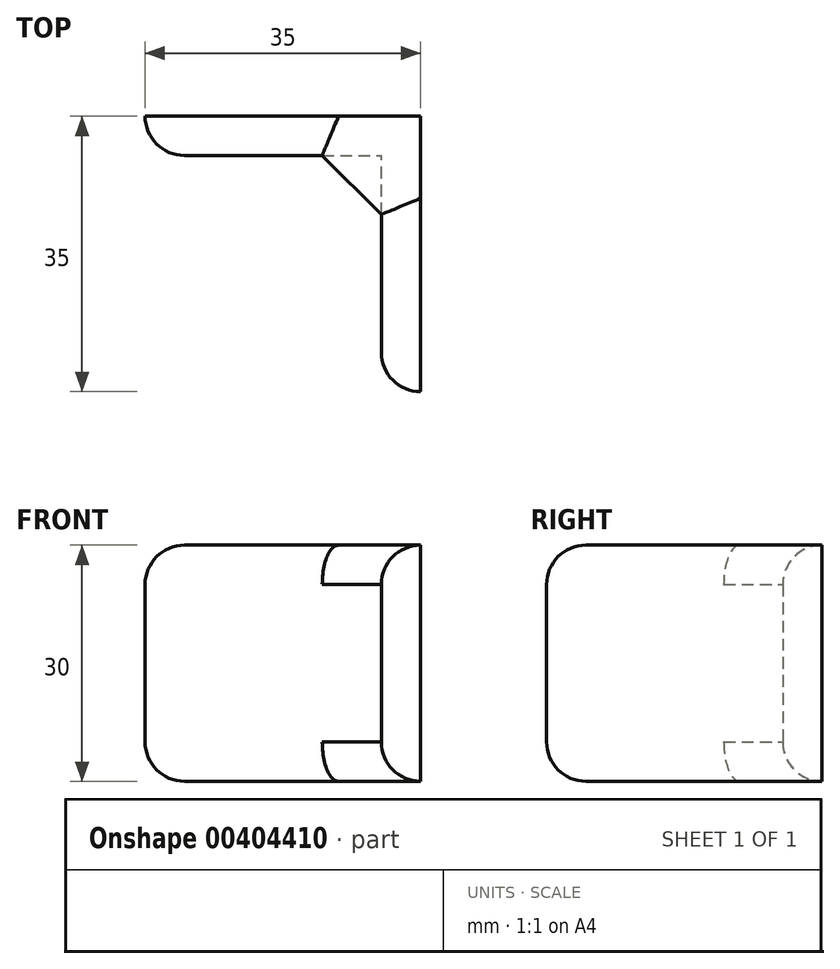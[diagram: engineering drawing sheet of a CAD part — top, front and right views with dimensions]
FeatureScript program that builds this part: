
annotation { "Feature Type Name" : "Feature", "Feature Type Description" : "" }
export const myFeature = defineFeature(function(context is Context, id is Id, definition is map)
    precondition{}
    {
        {
            var Q0;
            Q0=qCreatedBy(makeId("Front.planeOp"),FACE);
            var sketch = newSketch(context, id + "F0", { "sketchPlane" : qUnion([Q0])});
            skLineSegment(sketch, "E0.bottom", {"start": v(-19.46, -1.02) * mm, "end": v(15.54, -1.02) * mm});
            skLineSegment(sketch, "E0.top", {"start": v(-19.46, -21.02) * mm, "end": v(15.54, -21.02) * mm});
            skLineSegment(sketch, "E0.left", {"start": v(-19.46, -1.02) * mm, "end": v(-19.46, -21.02) * mm});
            skLineSegment(sketch, "E0.right", {"start": v(15.54, -1.02) * mm, "end": v(15.54, -21.02) * mm});
            skSolve(sketch);
        }
        {
            var Q0;
            Q0=makeQuery(id+"F0.imprint","IMPRINT",FACE,{"disambiguationData":[TD([[makeQuery(id+"F0.imprint","IMPRINT",EDGE,{"derivedFrom":sQuery(id+"F0.wireOp",EDGE,"E0.bottom")}),-1.0]])]});
            extrude(context, id + "F1", {"entities" : qUnion([Q0]), "depth" : 5 * mm});
        }
        {
            var Q0;
            Q0=makeQuery(id+"F1.opExtrude","CAP_FACE",FACE,{"disambiguationData":[OSD([sQuery(id+"F0.wireOp",EDGE,"E0.bottom"),sQuery(id+"F0.wireOp",EDGE,"E0.top"),sQuery(id+"F0.wireOp",EDGE,"E0.left"),sQuery(id+"F0.wireOp",EDGE,"E0.right")])],"isStart":false});
            var sketch = newSketch(context, id + "F2", { "sketchPlane" : qUnion([Q0])});
            skLineSegment(sketch, "E1.bottom", {"start": v(15.54, -1.02) * mm, "end": v(10.54, -1.02) * mm});
            skLineSegment(sketch, "E1.top", {"start": v(15.54, -21.02) * mm, "end": v(10.54, -21.02) * mm});
            skLineSegment(sketch, "E1.left", {"start": v(15.54, -1.02) * mm, "end": v(15.54, -21.02) * mm});
            skLineSegment(sketch, "E1.right", {"start": v(10.54, -1.02) * mm, "end": v(10.54, -21.02) * mm});
            skSolve(sketch);
        }
        {
            var Q0;
            Q0=makeQuery(id+"F2.imprint","IMPRINT",FACE,{"disambiguationData":[TD([[makeQuery(id+"F2.imprint","IMPRINT",EDGE,{"derivedFrom":sQuery(id+"F2.wireOp",EDGE,"E1.bottom")}),-1.0]])]});
            extrude(context, id + "F3", {"entities" : qUnion([Q0]), "operationType" : NewBodyOperationType.ADD, "depth" : 30 * mm});
        }
        {
            var Q0;
            Q0=makeQuery(id+"F1.opExtrude","CAP_EDGE",EDGE,{"disambiguationData":[OSD([sQuery(id+"F0.wireOp",EDGE,"E0.left")])],"isStart":false});
            var Q1;
            Q1=makeQuery(id+"F3.opExtrude","CAP_EDGE",EDGE,{"disambiguationData":[OSD([sQuery(id+"F2.wireOp",EDGE,"E1.right")])],"isStart":false});
            fillet(context, id + "F4", {"entities" : qUnion([Q0, Q1]), "radius" : 5 * mm, "tangentPropagation" : true, "allowEdgeOverflow" : false});
        }
        {
            var Q0;
            Q0=makeQuery(id+"F3.boolean.opBoolean","MERGE",FACE,{"derivedFrom":[makeQuery(id+"F1.opExtrude","SWEPT_FACE",FACE,{"disambiguationData":[OSD([sQuery(id+"F0.wireOp",EDGE,"E0.bottom")])]}),makeQuery(id+"F3.opExtrude","SWEPT_FACE",FACE,{"disambiguationData":[OSD([sQuery(id+"F2.wireOp",EDGE,"E1.bottom")])]})]});
            var sketch = newSketch(context, id + "F5", { "sketchPlane" : qUnion([Q0])});
            skLineSegment(sketch, "E2", {"start": v(15.54, 0) * mm, "end": v(-1.96, 0) * mm});
            skLineSegment(sketch, "E3", {"start": v(-1.96, 0) * mm, "end": v(15.54, -17.5) * mm});
            skSolve(sketch);
        }
        {
            var Q0;
            {var subQ0=sQuery(id+"F5.wireOp",EDGE,"E3");var subQ1=sQuery(id+"F0.wireOp",EDGE,"E0.bottom");var subQ2=makeQuery(id+"F1.opExtrude","CAP_EDGE",EDGE,{"disambiguationData":[OSD([subQ1])],"isStart":false});var subQ3=makeQuery(id+"F5.imprint","INTERSECT",VERTEX,{"derivedFrom":[subQ2,subQ0]});Q0=makeQuery(id+"F5.imprint","IMPRINT",FACE,{"disambiguationData":[TD([[makeQuery(id+"F5.imprint","IMPRINT",EDGE,{"disambiguationData":[TD([[subQ3,-1.0]])],"derivedFrom":subQ0}),1.0]])]});}
            var Q1;
            {var subQ0=sQuery(id+"F5.wireOp",EDGE,"E2");Q1=makeQuery(id+"F5.imprint","IMPRINT",FACE,{"disambiguationData":[TD([[makeQuery(id+"F5.imprint","IMPRINT",EDGE,{"derivedFrom":subQ0}),-1.0]])]});}
            extrude(context, id + "F6", {"entities" : qUnion([Q0, Q1]), "operationType" : NewBodyOperationType.ADD, "depth" : 5 * mm});
        }
        {
            var Q0;
            {var subQ1=sQuery(id+"F0.wireOp",EDGE,"E0.left");var subQ4=sQuery(id+"F0.wireOp",EDGE,"E0.bottom");var subQ6=sQuery(id+"F2.wireOp",EDGE,"E1.bottom");Q0=makeQuery(id+"F6.boolean.opBoolean","SPLIT",FACE,{"disambiguationData":[TD([makeQuery(id+"F4.opFillet","BLEND_FACE",FACE,{"disambiguationData":[OSD([subQ1])]})])],"derivedFrom":makeQuery(id+"F3.boolean.opBoolean","MERGE",FACE,{"derivedFrom":[makeQuery(id+"F1.opExtrude","SWEPT_FACE",FACE,{"disambiguationData":[OSD([subQ4])]}),makeQuery(id+"F3.opExtrude","SWEPT_FACE",FACE,{"disambiguationData":[OSD([subQ6])]})]})});}
            extrude(context, id + "F7", {"entities" : qUnion([Q0]), "operationType" : NewBodyOperationType.ADD, "depth" : 5 * mm});
        }
        {
            var Q0;
            {var subQ2=sQuery(id+"F0.wireOp",EDGE,"E0.right");var subQ4=sQuery(id+"F2.wireOp",EDGE,"E1.bottom");var subQ5=sQuery(id+"F0.wireOp",EDGE,"E0.bottom");Q0=makeQuery(id+"F6.boolean.opBoolean","SPLIT",FACE,{"disambiguationData":[TD([makeQuery(id+"F1.opExtrude","SWEPT_FACE",FACE,{"disambiguationData":[OSD([subQ2])]})])],"derivedFrom":makeQuery(id+"F3.boolean.opBoolean","MERGE",FACE,{"derivedFrom":[makeQuery(id+"F1.opExtrude","SWEPT_FACE",FACE,{"disambiguationData":[OSD([subQ5])]}),makeQuery(id+"F3.opExtrude","SWEPT_FACE",FACE,{"disambiguationData":[OSD([subQ4])]})]})});}
            extrude(context, id + "F8", {"entities" : qUnion([Q0]), "operationType" : NewBodyOperationType.ADD, "depth" : 5 * mm});
        }
        {
            var Q0;
            Q0=makeQuery(id+"F6.opExtrude","CAP_EDGE",EDGE,{"disambiguationData":[OSD([sQuery(id+"F5.wireOp",EDGE,"E3")])],"isStart":false});
            var Q1;
            {var subQ0=sQuery(id+"F0.wireOp",EDGE,"E0.bottom");Q1=makeQuery(id+"F7.opExtrude","CAP_EDGE",EDGE,{"disambiguationData":[OSD([subQ0]),TDD([makeQuery(id+"F6.boolean.opBoolean","SPLIT",EDGE,{"disambiguationData":[topologyDisambiguationEdgeConnected([makeQuery(id+"F1.opExtrude","SWEPT_FACE",FACE,{"disambiguationData":[OSD([subQ0])]})])],"derivedFrom":makeQuery(id+"F1.opExtrude","CAP_EDGE",EDGE,{"disambiguationData":[OSD([subQ0])],"isStart":false})})])],"isStart":false});}
            var Q2;
            {var subQ0=sQuery(id+"F0.wireOp",EDGE,"E0.bottom");var subQ1=sQuery(id+"F2.wireOp",EDGE,"E1.bottom");var subQ2=sQuery(id+"F2.wireOp",EDGE,"E1.right");Q2=makeQuery(id+"F8.opExtrude","CAP_EDGE",EDGE,{"disambiguationData":[OSD([subQ0,subQ1,subQ2]),TDD([makeQuery(id+"F6.boolean.opBoolean","SPLIT",EDGE,{"disambiguationData":[topologyDisambiguationEdgeConnected([makeQuery(id+"F1.opExtrude","SWEPT_FACE",FACE,{"disambiguationData":[OSD([subQ0])]})])],"derivedFrom":makeQuery(id+"F3.opExtrude","SWEPT_EDGE",EDGE,{"disambiguationData":[OSD([subQ0,subQ1,subQ2])]})})])],"isStart":false});}
            fillet(context, id + "F9", {"entities" : qUnion([Q0, Q1, Q2]), "radius" : 5 * mm, "tangentPropagation" : true, "allowEdgeOverflow" : false});
        }
        {
            var Q0;
            Q0=makeQuery(id+"F3.boolean.opBoolean","MERGE",FACE,{"derivedFrom":[makeQuery(id+"F1.opExtrude","SWEPT_FACE",FACE,{"disambiguationData":[OSD([sQuery(id+"F0.wireOp",EDGE,"E0.top")])]}),makeQuery(id+"F3.opExtrude","SWEPT_FACE",FACE,{"disambiguationData":[OSD([sQuery(id+"F2.wireOp",EDGE,"E1.top")])]})]});
            var sketch = newSketch(context, id + "F10", { "sketchPlane" : qUnion([Q0])});
            skLineSegment(sketch, "E4", {"start": v(-1.96, 0) * mm, "end": v(15.54, 17.5) * mm});
            skSolve(sketch);
        }
        {
            var Q0;
            {var subQ1=sQuery(id+"F0.wireOp",EDGE,"E0.top");var subQ3=makeQuery(id+"F1.opExtrude","CAP_EDGE",EDGE,{"disambiguationData":[OSD([subQ1])],"isStart":true});var subQ5=sQuery(id+"F10.wireOp",EDGE,"E4");var subQ9=makeQuery(id+"F10.imprint","INTERSECT",VERTEX,{"derivedFrom":[subQ3,subQ5]});Q0=makeQuery(id+"F10.imprint","IMPRINT",FACE,{"disambiguationData":[TD([[makeQuery(id+"F10.imprint","IMPRINT",EDGE,{"disambiguationData":[TD([[subQ9,-1.0]])],"derivedFrom":subQ5}),-1.0]])]});}
            var Q1;
            {var subQ1=sQuery(id+"F0.wireOp",EDGE,"E0.top");var subQ6=makeQuery(id+"F4.opFillet","BLEND_EDGE",EDGE,{"blendedFrom":[makeQuery(id+"F1.opExtrude","CAP_EDGE",EDGE,{"disambiguationData":[OSD([sQuery(id+"F0.wireOp",EDGE,"E0.left")])],"isStart":false}),makeQuery(id+"F3.boolean.opBoolean","MERGE",FACE,{"derivedFrom":[makeQuery(id+"F1.opExtrude","SWEPT_FACE",FACE,{"disambiguationData":[OSD([subQ1])]}),makeQuery(id+"F3.opExtrude","SWEPT_FACE",FACE,{"disambiguationData":[OSD([sQuery(id+"F2.wireOp",EDGE,"E1.top")])]})]})],"blendedInto":[makeQuery(id+"F3.boolean.opBoolean","MERGE",FACE,{"derivedFrom":[makeQuery(id+"F1.opExtrude","SWEPT_FACE",FACE,{"disambiguationData":[OSD([subQ1])]}),makeQuery(id+"F3.opExtrude","SWEPT_FACE",FACE,{"disambiguationData":[OSD([sQuery(id+"F2.wireOp",EDGE,"E1.top")])]})]})]});Q1=makeQuery(id+"F10.imprint","IMPRINT",FACE,{"disambiguationData":[TD([[makeQuery(id+"F10.imprint","IMPRINT",EDGE,{"derivedFrom":subQ6}),1.0]])]});}
            var Q2;
            {var subQ0=sQuery(id+"F10.wireOp",EDGE,"E4");var subQ1=sQuery(id+"F0.wireOp",EDGE,"E0.top");var subQ2=makeQuery(id+"F1.opExtrude","CAP_EDGE",EDGE,{"disambiguationData":[OSD([subQ1])],"isStart":false});var subQ3=makeQuery(id+"F10.imprint","INTERSECT",VERTEX,{"derivedFrom":[subQ2,subQ0]});Q2=makeQuery(id+"F10.imprint","IMPRINT",FACE,{"disambiguationData":[TD([[makeQuery(id+"F10.imprint","IMPRINT",EDGE,{"disambiguationData":[TD([[subQ3,-1.0]])],"derivedFrom":subQ0}),-1.0]])]});}
            var Q3;
            {var subQ1=sQuery(id+"F2.wireOp",EDGE,"E1.top");var subQ2=sQuery(id+"F0.wireOp",EDGE,"E0.top");var subQ5=sQuery(id+"F2.wireOp",EDGE,"E1.right");var subQ8=makeQuery(id+"F4.opFillet","BLEND_EDGE",EDGE,{"blendedFrom":[makeQuery(id+"F3.opExtrude","CAP_EDGE",EDGE,{"disambiguationData":[OSD([subQ5])],"isStart":false}),makeQuery(id+"F3.boolean.opBoolean","MERGE",FACE,{"derivedFrom":[makeQuery(id+"F1.opExtrude","SWEPT_FACE",FACE,{"disambiguationData":[OSD([subQ2])]}),makeQuery(id+"F3.opExtrude","SWEPT_FACE",FACE,{"disambiguationData":[OSD([subQ1])]})]})],"blendedInto":[makeQuery(id+"F3.boolean.opBoolean","MERGE",FACE,{"derivedFrom":[makeQuery(id+"F1.opExtrude","SWEPT_FACE",FACE,{"disambiguationData":[OSD([subQ2])]}),makeQuery(id+"F3.opExtrude","SWEPT_FACE",FACE,{"disambiguationData":[OSD([subQ1])]})]})]});Q3=makeQuery(id+"F10.imprint","IMPRINT",FACE,{"disambiguationData":[TD([[makeQuery(id+"F10.imprint","IMPRINT",EDGE,{"derivedFrom":subQ8}),1.0]])]});}
            extrude(context, id + "F11", {"entities" : qUnion([Q0, Q1, Q2, Q3]), "operationType" : NewBodyOperationType.ADD, "depth" : 5 * mm});
        }
        {
            var Q0;
            Q0=makeQuery(id+"F11.opExtrude","CAP_EDGE",EDGE,{"disambiguationData":[OSD([sQuery(id+"F0.wireOp",EDGE,"E0.top"),sQuery(id+"F0.wireOp",EDGE,"E0.left"),sQuery(id+"F2.wireOp",EDGE,"E1.top")])],"isStart":false});
            var Q1;
            {var subQ0=sQuery(id+"F0.wireOp",EDGE,"E0.top");var subQ1=makeQuery(id+"F1.opExtrude","CAP_EDGE",EDGE,{"disambiguationData":[OSD([subQ0])],"isStart":false});Q1=makeQuery(id+"F11.opExtrude","CAP_EDGE",EDGE,{"disambiguationData":[OSD([subQ0]),TDD([makeQuery(id+"F10.imprint","IMPRINT",EDGE,{"disambiguationData":[TD([[makeQuery(id+"F10.imprint","INTERSECT",VERTEX,{"derivedFrom":[subQ1,sQuery(id+"F10.wireOp",EDGE,"E4")]}),1.0]])],"derivedFrom":subQ1})])],"isStart":false});}
            var Q2;
            Q2=makeQuery(id+"F11.opExtrude","CAP_EDGE",EDGE,{"disambiguationData":[OSD([sQuery(id+"F10.wireOp",EDGE,"E4")])],"isStart":false});
            var Q3;
            {var subQ0=sQuery(id+"F2.wireOp",EDGE,"E1.top");var subQ1=sQuery(id+"F0.wireOp",EDGE,"E0.top");var subQ2=sQuery(id+"F2.wireOp",EDGE,"E1.right");var subQ3=makeQuery(id+"F3.opExtrude","SWEPT_EDGE",EDGE,{"disambiguationData":[OSD([subQ1,subQ0,subQ2])]});Q3=makeQuery(id+"F11.opExtrude","CAP_EDGE",EDGE,{"disambiguationData":[OSD([subQ1,subQ0,subQ2]),TDD([makeQuery(id+"F10.imprint","IMPRINT",EDGE,{"disambiguationData":[TD([[makeQuery(id+"F10.imprint","INTERSECT",VERTEX,{"derivedFrom":[subQ3,sQuery(id+"F10.wireOp",EDGE,"E4")]}),1.0]])],"derivedFrom":subQ3})])],"isStart":false});}
            var Q4;
            {var subQ0=sQuery(id+"F2.wireOp",EDGE,"E1.top");var subQ1=sQuery(id+"F0.wireOp",EDGE,"E0.top");var subQ2=sQuery(id+"F2.wireOp",EDGE,"E1.right");Q4=makeQuery(id+"F11.opExtrude","CAP_EDGE",EDGE,{"disambiguationData":[OSD([subQ1,subQ0,subQ2]),TDD([makeQuery(id+"F10.imprint","IMPRINT",EDGE,{"derivedFrom":makeQuery(id+"F4.opFillet","BLEND_EDGE",EDGE,{"blendedFrom":[makeQuery(id+"F3.opExtrude","CAP_EDGE",EDGE,{"disambiguationData":[OSD([subQ2])],"isStart":false}),makeQuery(id+"F3.boolean.opBoolean","MERGE",FACE,{"derivedFrom":[makeQuery(id+"F1.opExtrude","SWEPT_FACE",FACE,{"disambiguationData":[OSD([subQ1])]}),makeQuery(id+"F3.opExtrude","SWEPT_FACE",FACE,{"disambiguationData":[OSD([subQ0])]})]})],"blendedInto":[makeQuery(id+"F3.boolean.opBoolean","MERGE",FACE,{"derivedFrom":[makeQuery(id+"F1.opExtrude","SWEPT_FACE",FACE,{"disambiguationData":[OSD([subQ1])]}),makeQuery(id+"F3.opExtrude","SWEPT_FACE",FACE,{"disambiguationData":[OSD([subQ0])]})]})]})})])],"isStart":false});}
            fillet(context, id + "F12", {"entities" : qUnion([Q0, Q1, Q2, Q3, Q4]), "radius" : 5 * mm, "tangentPropagation" : true, "allowEdgeOverflow" : false});
        }
    });
